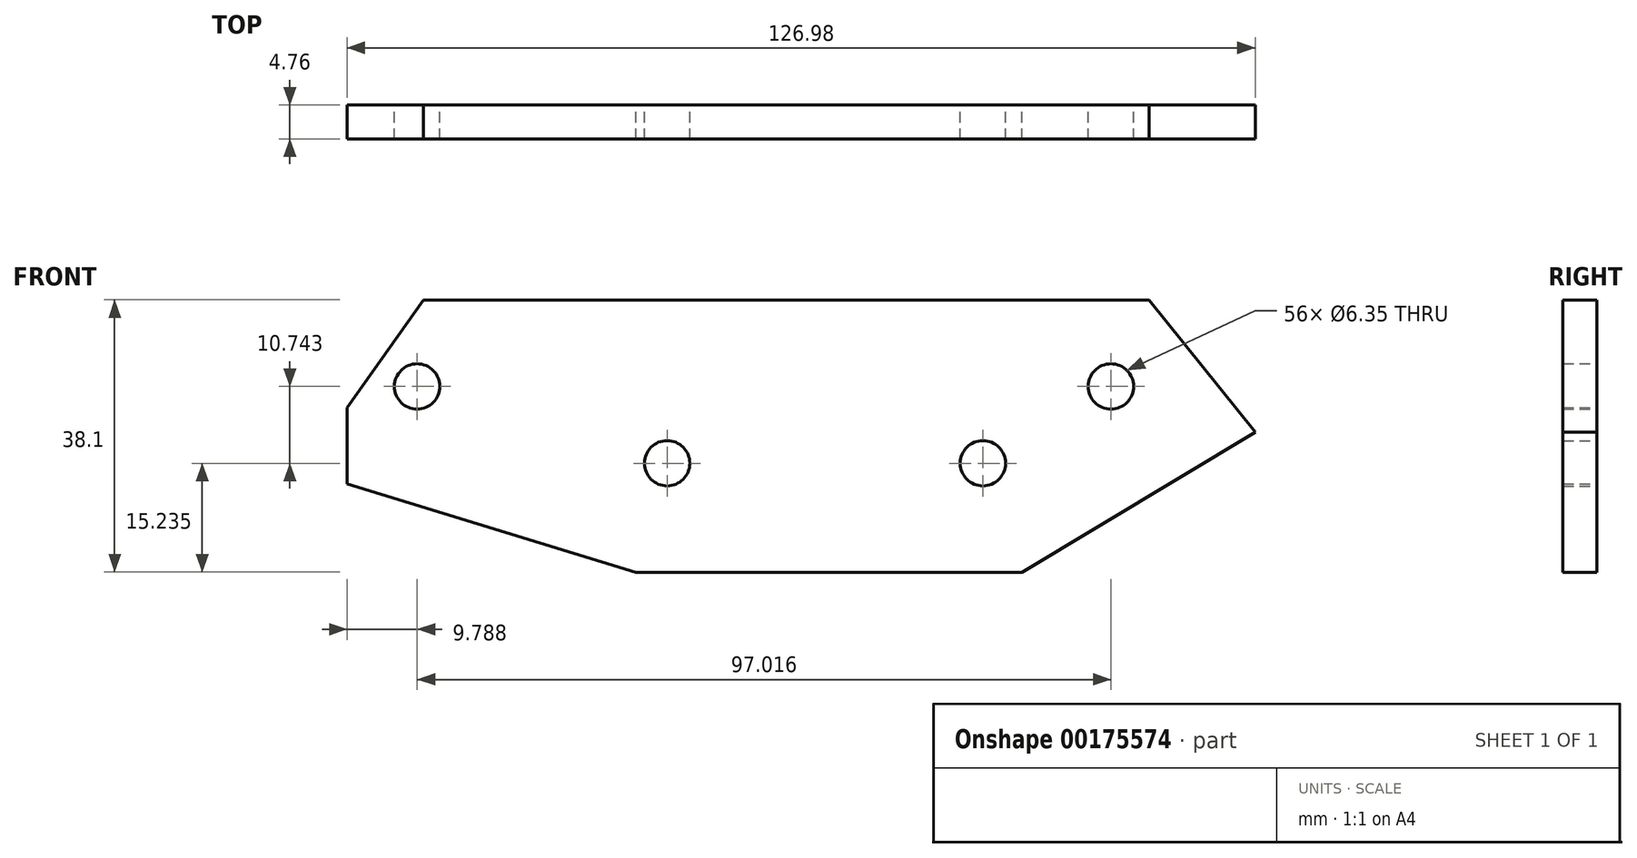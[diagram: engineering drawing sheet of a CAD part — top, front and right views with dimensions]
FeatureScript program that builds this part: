
annotation { "Feature Type Name" : "Feature", "Feature Type Description" : "" }
export const myFeature = defineFeature(function(context is Context, id is Id, definition is map)
    precondition{}
    {
        {
            var Q0;
            Q0=qCreatedBy(makeId("Front.planeOp"),FACE);
            var sketch = newSketch(context, id + "F0", { "sketchPlane" : qUnion([Q0])});
            skLineSegment(sketch, "E0.bottom", {"start": v(62.38, 23.07) * mm, "end": v(-64.62, 23.07) * mm});
            skLineSegment(sketch, "E0.top", {"start": v(62.38, -15.03) * mm, "end": v(-64.62, -15.03) * mm});
            skLineSegment(sketch, "E0.left", {"start": v(62.38, 23.07) * mm, "end": v(62.38, -15.03) * mm});
            skLineSegment(sketch, "E0.right", {"start": v(-64.62, 23.07) * mm, "end": v(-64.62, -15.03) * mm});
            skPoint(sketch, "E0.middle", {"position": v(-1.12, 4.02) * mm});
            skLineSegment(sketch, "E1", {"start": v(-0.82, 0.2) * mm, "end": v(24.28, 0.2) * mm});
            skLineSegment(sketch, "E2", {"start": v(-0.82, 0.2) * mm, "end": v(-19.87, 0.2) * mm});
            skLineSegment(sketch, "E3", {"start": v(24.28, 0.2) * mm, "end": v(48.07, 26.63) * mm});
            skLineSegment(sketch, "E4", {"start": v(62.38, 23.07) * mm, "end": v(-1.12, -15.03) * mm});
            skLineSegment(sketch, "E5", {"start": v(-1.12, -15.03) * mm, "end": v(-1.12, -5.5) * mm});
            skLineSegment(sketch, "E6", {"start": v(-1.12, -5.5) * mm, "end": v(-54.83, 10.95) * mm});
            skLineSegment(sketch, "E7", {"start": v(-1.12, -5.5) * mm, "end": v(9.39, -8.73) * mm});
            skCircle(sketch, "E8", {"center": v(-19.87, 0.2) * mm, "radius": 3.18 * mm});
            skCircle(sketch, "E9", {"center": v(24.28, 0.2) * mm, "radius": 3.18 * mm});
            skCircle(sketch, "E10", {"center": v(-54.83, 10.95) * mm, "radius": 3.18 * mm});
            skCircle(sketch, "E11", {"center": v(42.18, 10.95) * mm, "radius": 3.18 * mm});
            skLineSegment(sketch, "E12", {"start": v(-64.62, -2.66) * mm, "end": v(-24.22, -15.03) * mm});
            skLineSegment(sketch, "E13", {"start": v(62.38, 4.55) * mm, "end": v(29.73, -15.03) * mm});
            skLineSegment(sketch, "E14", {"start": v(47.55, 23.07) * mm, "end": v(62.38, 4.52) * mm});
            skLineSegment(sketch, "E15", {"start": v(-53.97, 23.07) * mm, "end": v(-64.62, 7.99) * mm});
            skSolve(sketch);
        }
        {
            var Q0;
            {var subQ1=sQuery(id+"F0.wireOp",EDGE,"E5");Q0=makeQuery(id+"F0.imprint","IMPRINT",FACE,{"disambiguationData":[TD([[makeQuery(id+"F0.imprint","IMPRINT",EDGE,{"derivedFrom":subQ1}),1.0]])]});}
            var Q1;
            {var subQ0=sQuery(id+"F0.wireOp",EDGE,"E7");Q1=makeQuery(id+"F0.imprint","IMPRINT",FACE,{"disambiguationData":[TD([[makeQuery(id+"F0.imprint","IMPRINT",EDGE,{"derivedFrom":subQ0}),1.0]])]});}
            var Q2;
            {var subQ0=sQuery(id+"F0.wireOp",EDGE,"E3");var subQ1=sQuery(id+"F0.wireOp",EDGE,"E0.bottom");var subQ2=makeQuery(id+"F0.imprint","INTERSECT",VERTEX,{"derivedFrom":[subQ1,subQ0]});Q2=makeQuery(id+"F0.imprint","IMPRINT",FACE,{"disambiguationData":[TD([[makeQuery(id+"F0.imprint","IMPRINT",EDGE,{"disambiguationData":[TD([[subQ2,1.0]])],"derivedFrom":subQ0}),-1.0]])]});}
            var Q3;
            {var subQ0=sQuery(id+"F0.wireOp",EDGE,"E5");Q3=makeQuery(id+"F0.imprint","IMPRINT",FACE,{"disambiguationData":[TD([[makeQuery(id+"F0.imprint","IMPRINT",EDGE,{"derivedFrom":subQ0}),-1.0]])]});}
            var Q4;
            {var subQ0=sQuery(id+"F0.wireOp",EDGE,"E4");var subQ7=sQuery(id+"F0.wireOp",EDGE,"E14");var subQ8=makeQuery(id+"F0.imprint","INTERSECT",VERTEX,{"derivedFrom":[subQ0,subQ7]});Q4=makeQuery(id+"F0.imprint","IMPRINT",FACE,{"disambiguationData":[TD([[makeQuery(id+"F0.imprint","IMPRINT",EDGE,{"disambiguationData":[TD([[subQ8,-1.0]])],"derivedFrom":subQ0}),1.0]])]});}
            extrude(context, id + "F1", {"entities" : qUnion([Q0, Q1, Q2, Q3, Q4]), "depth" : 4.76 * mm});
        }
    });
